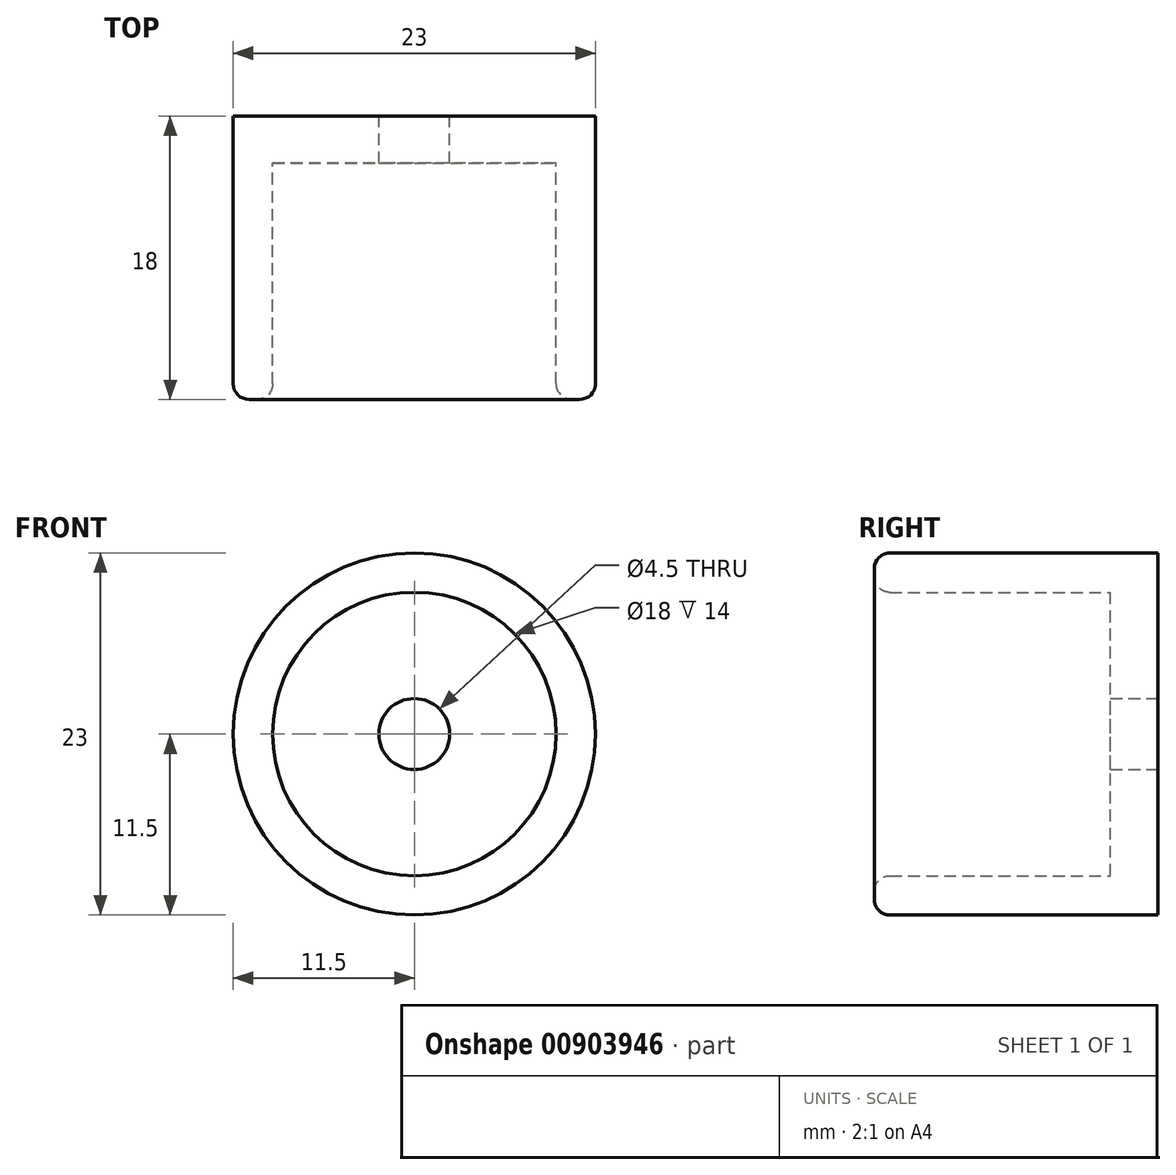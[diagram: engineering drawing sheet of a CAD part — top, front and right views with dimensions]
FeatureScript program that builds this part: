
annotation { "Feature Type Name" : "Feature", "Feature Type Description" : "" }
export const myFeature = defineFeature(function(context is Context, id is Id, definition is map)
    precondition{}
    {
        {
            var Q0;
            Q0=qCreatedBy(makeId("Front.planeOp"),FACE);
            var sketch = newSketch(context, id + "F0", { "sketchPlane" : qUnion([Q0])});
            skCircle(sketch, "E0", {"center": v(0, 0) * mm, "radius": 11.5 * mm});
            skCircle(sketch, "E1", {"center": v(0, 0) * mm, "radius": 9 * mm});
            skCircle(sketch, "E2", {"center": v(0, 0) * mm, "radius": 2.25 * mm});
            skSolve(sketch);
        }
        {
            var Q0;
            Q0=makeQuery(id+"F0.imprint","IMPRINT",FACE,{"disambiguationData":[TD([[makeQuery(id+"F0.imprint","IMPRINT",EDGE,{"derivedFrom":sQuery(id+"F0.wireOp",EDGE,"E1")}),1.0]])]});
            extrude(context, id + "F1", {"entities" : qUnion([Q0]), "depth" : 3 * mm, "offsetDistance" : 25 * mm});
        }
        {
            var Q0;
            Q0=makeQuery(id+"F0.imprint","IMPRINT",FACE,{"disambiguationData":[TD([[makeQuery(id+"F0.imprint","IMPRINT",EDGE,{"derivedFrom":sQuery(id+"F0.wireOp",EDGE,"E0")}),1.0]])]});
            extrude(context, id + "F2", {"entities" : qUnion([Q0]), "operationType" : NewBodyOperationType.ADD, "depth" : 18 * mm, "offsetDistance" : 25 * mm});
        }
        {
            var Q0;
            Q0=makeQuery(id+"F2.opExtrude","CAP_EDGE",EDGE,{"disambiguationData":[OSD([sQuery(id+"F0.wireOp",EDGE,"E1")])],"isStart":false});
            var Q1;
            Q1=makeQuery(id+"F2.opExtrude","CAP_EDGE",EDGE,{"disambiguationData":[OSD([sQuery(id+"F0.wireOp",EDGE,"E0")])],"isStart":false});
            fillet(context, id + "F3", {"entities" : qUnion([Q0, Q1]), "radius" : 1 * mm, "tangentPropagation" : true, "allowEdgeOverflow" : false});
        }
    });
